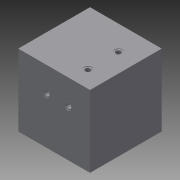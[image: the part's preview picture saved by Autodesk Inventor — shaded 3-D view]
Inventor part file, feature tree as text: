
AUTODESK INVENTOR PART (.ipt)
format: ipt  version: 2014 (Build 180170000, 170)  size: 275,968 bytes
history: native  units: mm
features: other x48, sketch x7, extrude x1
ambient origin geometry x8: Origin, YZ Plane, XZ Plane, XY Plane, X Axis, Y Axis, Z Axis, Center Point
bodies: Body1 (feature_tree)
feature tree (56):
  extrude  "拉伸1"  TaperAngle=0.0deg  [1 undecoded]
  other  "UCS1"
  other  "UCS2"
  other  "UCS3"
  other  "UCS4"
  other  "UCS5"
  other  "UCS6"
  sketch  "草图1"  dims[d0=300.0mm d1=0.0mm]
  other  "UCS1: YZ 平面"
  other  "UCS1: XZ 平面"
  other  "UCS1: XY 平面"
  other  "UCS1: X 轴"
  other  "UCS1: Y 轴"
  other  "UCS1: Z 轴"
  other  "UCS1: 原点"
  other  "UCS2: YZ 平面"
  other  "UCS2: XZ 平面"
  other  "UCS2: XY 平面"
  other  "UCS2: X 轴"
  other  "UCS2: Y 轴"
  other  "UCS2: Z 轴"
  other  "UCS2: 原点"
  other  "UCS3: YZ 平面"
  other  "UCS3: XZ 平面"
  other  "UCS3: XY 平面"
  other  "UCS3: X 轴"
  other  "UCS3: Y 轴"
  other  "UCS3: Z 轴"
  other  "UCS3: 原点"
  other  "UCS4: YZ 平面"
  other  "UCS4: XZ 平面"
  other  "UCS4: XY 平面"
  other  "UCS4: X 轴"
  other  "UCS4: Y 轴"
  other  "UCS4: Z 轴"
  other  "UCS4: 原点"
  other  "UCS5: YZ 平面"
  other  "UCS5: XZ 平面"
  other  "UCS5: XY 平面"
  other  "UCS5: X 轴"
  other  "UCS5: Y 轴"
  other  "UCS5: Z 轴"
  other  "UCS5: 原点"
  other  "UCS6: YZ 平面"
  other  "UCS6: XZ 平面"
  other  "UCS6: XY 平面"
  other  "UCS6: X 轴"
  other  "UCS6: Y 轴"
  other  "UCS6: Z 轴"
  other  "UCS6: 原点"
  sketch  "草图2"  dims[d2=0.0mm d3=0.0mm d4=0.0mm d5=0.0mm d6=0.0mm d7=0.0mm]
  sketch  "草图3"  dims[d8=0.0mm d9=0.0mm d10=0.0mm d11=0.0mm d12=0.0mm d13=0.0mm]
  sketch  "草图4"  dims[d14=0.0mm d15=0.0mm d16=0.0mm d17=0.0mm d18=0.0mm d19=0.0mm]
  sketch  "草图6"  dims[d20=0.0mm d21=0.0mm d22=0.0mm d23=0.0mm d24=0.0mm d25=0.0mm]
  sketch  "草图7"  dims[d26=0.0mm d27=0.0mm d28=0.0mm d29=0.0mm d30=0.0mm d31=0.0mm]
  sketch  "草图8"  dims[d32=0.0mm d33=0.0mm d34=0.0mm d35=0.0mm d36=0.0mm d37=0.0mm d38=0.0mm d42=0.0mm d46=0.0mm d53=0.0mm d57=0.0mm d61=0.0mm]
note: 1 required parameter value undecoded (feature->parameter linkage not recoverable at this tier; creation-order binding heuristic only, values carry confidence <= 0.55)
